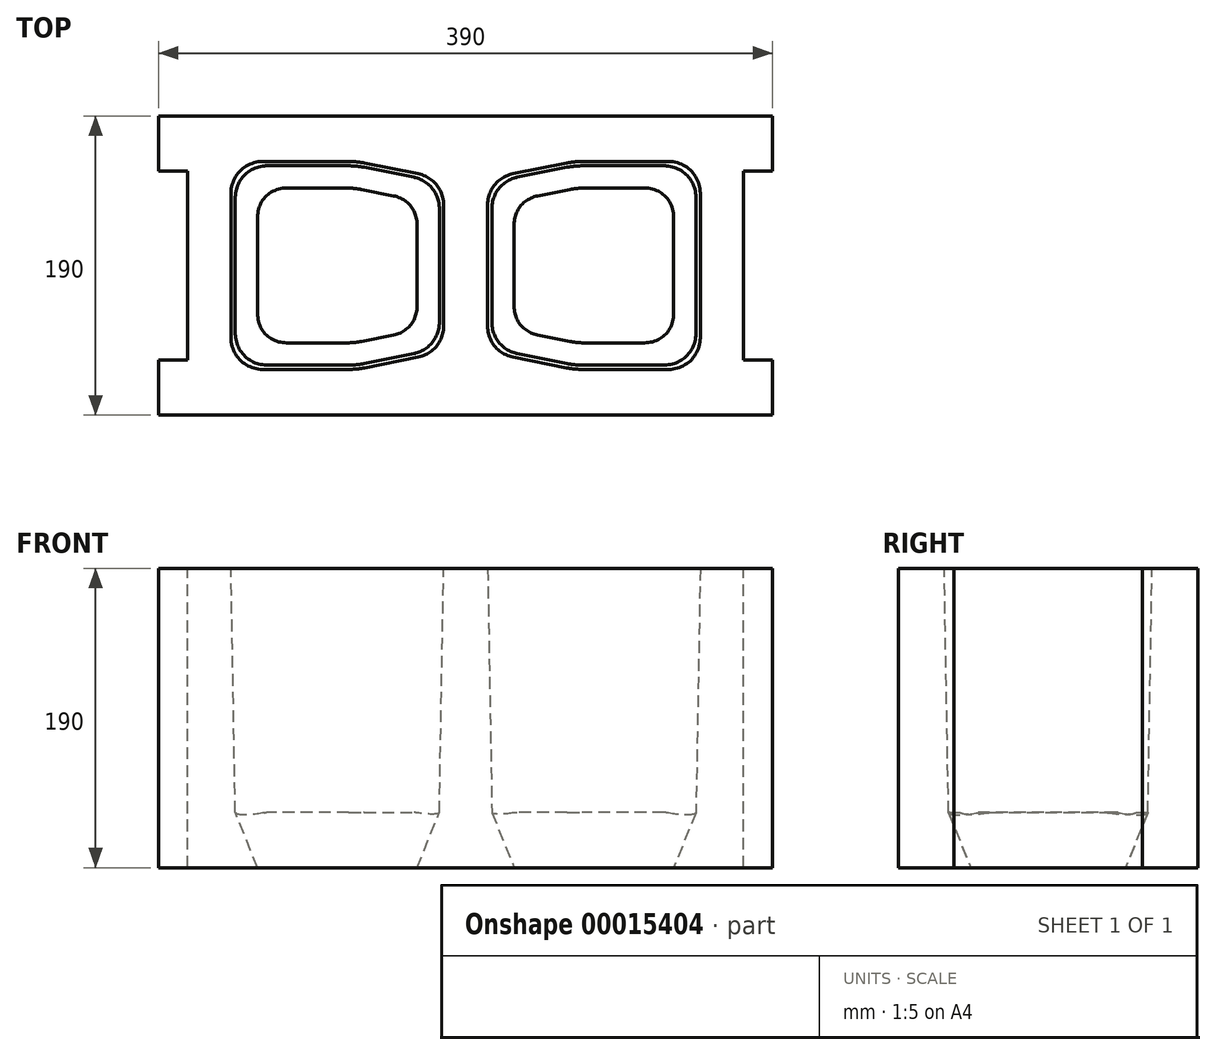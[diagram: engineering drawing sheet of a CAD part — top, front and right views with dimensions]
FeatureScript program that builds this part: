
annotation { "Feature Type Name" : "Feature", "Feature Type Description" : "" }
export const myFeature = defineFeature(function(context is Context, id is Id, definition is map)
    precondition{}
    {
        {
            var Q0;
            Q0=qCreatedBy(makeId("Top.planeOp"),FACE);
            var sketch = newSketch(context, id + "F0", { "sketchPlane" : qUnion([Q0])});
            skLineSegment(sketch, "E0.bottom", {"start": v(-195, 95) * mm, "end": v(195, 95) * mm});
            skLineSegment(sketch, "E0.top", {"start": v(-195, -95) * mm, "end": v(195, -95) * mm});
            skLineSegment(sketch, "E0.left", {"start": v(-195, 95) * mm, "end": v(-195, -95) * mm});
            skLineSegment(sketch, "E0.right", {"start": v(195, 95) * mm, "end": v(195, -95) * mm});
            skSolve(sketch);
        }
        {
            var Q0;
            Q0=qSketchRegion(id+"F0",true);
            extrude(context, id + "F1", {"entities" : qUnion([Q0]), "depth" : 190 * mm});
        }
        {
            var Q0;
            Q0=makeQuery(id+"F1.opExtrude","CAP_FACE",FACE,{"disambiguationData":[OSD([sQuery(id+"F0.wireOp",EDGE,"E0.bottom"),sQuery(id+"F0.wireOp",EDGE,"E0.top"),sQuery(id+"F0.wireOp",EDGE,"E0.left"),sQuery(id+"F0.wireOp",EDGE,"E0.right")])],"isStart":false});
            var sketch = newSketch(context, id + "F2", { "sketchPlane" : qUnion([Q0])});
            skLineSegment(sketch, "E1.bottom", {"start": v(-195, 83) * mm, "end": v(-191, 83) * mm});
            skLineSegment(sketch, "E1.top", {"start": v(-195, 71) * mm, "end": v(-191, 71) * mm});
            skLineSegment(sketch, "E1.left", {"start": v(-195, 83) * mm, "end": v(-195, 71) * mm});
            skLineSegment(sketch, "E1.right", {"start": v(-191, 83) * mm, "end": v(-191, 71) * mm});
            skSolve(sketch);
        }
        {
            var Q0;
            Q0=makeQuery(id+"F1.opExtrude","CAP_FACE",FACE,{"disambiguationData":[OSD([sQuery(id+"F0.wireOp",EDGE,"E0.bottom"),sQuery(id+"F0.wireOp",EDGE,"E0.top"),sQuery(id+"F0.wireOp",EDGE,"E0.left"),sQuery(id+"F0.wireOp",EDGE,"E0.right")])],"isStart":false});
            var sketch = newSketch(context, id + "F3", { "sketchPlane" : qUnion([Q0])});
            skLineSegment(sketch, "E2.bottom", {"start": v(-195, -71) * mm, "end": v(-191, -71) * mm});
            skLineSegment(sketch, "E2.top", {"start": v(-195, -83) * mm, "end": v(-191, -83) * mm});
            skLineSegment(sketch, "E2.left", {"start": v(-195, -71) * mm, "end": v(-195, -83) * mm});
            skLineSegment(sketch, "E2.right", {"start": v(-191, -71) * mm, "end": v(-191, -83) * mm});
            skLineSegment(sketch, "E3.MirrorCS", {"start": v(195, -83) * mm, "end": v(191, -83) * mm});
            skLineSegment(sketch, "E4.MirrorCS", {"start": v(195, -71) * mm, "end": v(191, -71) * mm});
            skLineSegment(sketch, "E5.MirrorCS", {"start": v(191, -71) * mm, "end": v(191, -83) * mm});
            skLineSegment(sketch, "E6.MirrorCS", {"start": v(195, -71) * mm, "end": v(195, -83) * mm});
            skLineSegment(sketch, "E7.MirrorCS", {"start": v(195, 71) * mm, "end": v(191, 71) * mm});
            skLineSegment(sketch, "E8.MirrorCS", {"start": v(191, 71) * mm, "end": v(191, 83) * mm});
            skLineSegment(sketch, "E9.MirrorCS", {"start": v(195, 71) * mm, "end": v(195, 83) * mm});
            skLineSegment(sketch, "E10.MirrorCS", {"start": v(195, 83) * mm, "end": v(191, 83) * mm});
            skSolve(sketch);
        }
        {
            var Q0;
            Q0=makeQuery(id+"F1.opExtrude","CAP_FACE",FACE,{"disambiguationData":[OSD([sQuery(id+"F0.wireOp",EDGE,"E0.bottom"),sQuery(id+"F0.wireOp",EDGE,"E0.top"),sQuery(id+"F0.wireOp",EDGE,"E0.left"),sQuery(id+"F0.wireOp",EDGE,"E0.right")])],"isStart":false});
            var sketch = newSketch(context, id + "F4", { "sketchPlane" : qUnion([Q0])});
            skLineSegment(sketch, "E11.bottom", {"start": v(-195, 60) * mm, "end": v(-176.5, 60) * mm});
            skLineSegment(sketch, "E11.top", {"start": v(-195, -60) * mm, "end": v(-176.5, -60) * mm});
            skLineSegment(sketch, "E11.left", {"start": v(-195, 60) * mm, "end": v(-195, -60) * mm});
            skLineSegment(sketch, "E11.right", {"start": v(-176.5, 60) * mm, "end": v(-176.5, -60) * mm});
            skLineSegment(sketch, "E12.MirrorCS", {"start": v(195, 60) * mm, "end": v(176.5, 60) * mm});
            skLineSegment(sketch, "E13.MirrorCS", {"start": v(195, -60) * mm, "end": v(176.5, -60) * mm});
            skLineSegment(sketch, "E14.MirrorCS", {"start": v(195, 60) * mm, "end": v(195, -60) * mm});
            skLineSegment(sketch, "E15.MirrorCS", {"start": v(176.5, 60) * mm, "end": v(176.5, -60) * mm});
            skSolve(sketch);
        }
        {
            var Q0;
            Q0=makeQuery(id+"F4.imprint","IMPRINT",FACE,{"disambiguationData":[TD([[makeQuery(id+"F4.imprint","IMPRINT",EDGE,{"derivedFrom":sQuery(id+"F4.wireOp",EDGE,"E12.MirrorCS")}),1.0]])]});
            var Q1;
            Q1=makeQuery(id+"F4.imprint","IMPRINT",FACE,{"disambiguationData":[TD([[makeQuery(id+"F4.imprint","IMPRINT",EDGE,{"derivedFrom":sQuery(id+"F4.wireOp",EDGE,"E11.bottom")}),-1.0]])]});
            extrude(context, id + "F5", {"entities" : qUnion([Q0, Q1]), "operationType" : NewBodyOperationType.REMOVE, "endBound" : BoundingType.THROUGH_ALL, "oppositeDirection" : true, "depth" : 25 * mm});
        }
        {
            var Q0;
            Q0=makeQuery(id+"F1.opExtrude","CAP_FACE",FACE,{"disambiguationData":[OSD([sQuery(id+"F0.wireOp",EDGE,"E0.bottom"),sQuery(id+"F0.wireOp",EDGE,"E0.top"),sQuery(id+"F0.wireOp",EDGE,"E0.left"),sQuery(id+"F0.wireOp",EDGE,"E0.right")])],"isStart":false});
            var sketch = newSketch(context, id + "F6", { "sketchPlane" : qUnion([Q0])});
            skLineSegment(sketch, "E16", {"start": v(-149, 66) * mm, "end": v(-149, -66) * mm});
            skLineSegment(sketch, "E17", {"start": v(-149, -66) * mm, "end": v(-69, -66) * mm});
            skLineSegment(sketch, "E18", {"start": v(-69, -66) * mm, "end": v(-14, -55) * mm});
            skLineSegment(sketch, "E19", {"start": v(-14, -55) * mm, "end": v(-14, 55) * mm});
            skLineSegment(sketch, "E20", {"start": v(-14, 55) * mm, "end": v(-69, 66) * mm});
            skLineSegment(sketch, "E21", {"start": v(-69, 66) * mm, "end": v(-149, 66) * mm});
            skLineSegment(sketch, "E22.MirrorCS", {"start": v(149, 66) * mm, "end": v(149, -66) * mm});
            skLineSegment(sketch, "E23.MirrorCS", {"start": v(149, -66) * mm, "end": v(69, -66) * mm});
            skLineSegment(sketch, "E24.MirrorCS", {"start": v(69, -66) * mm, "end": v(14, -55) * mm});
            skLineSegment(sketch, "E25.MirrorCS", {"start": v(69, 66) * mm, "end": v(149, 66) * mm});
            skLineSegment(sketch, "E26.MirrorCS", {"start": v(14, 55) * mm, "end": v(69, 66) * mm});
            skLineSegment(sketch, "E27.MirrorCS", {"start": v(14, -55) * mm, "end": v(14, 55) * mm});
            skSolve(sketch);
        }
        {
            var Q0;
            Q0=makeQuery(id+"F6.imprint","IMPRINT",FACE,{"disambiguationData":[TD([[makeQuery(id+"F6.imprint","IMPRINT",EDGE,{"derivedFrom":sQuery(id+"F6.wireOp",EDGE,"E22.MirrorCS")}),-1.0]])]});
            var Q1;
            Q1=makeQuery(id+"F6.imprint","IMPRINT",FACE,{"disambiguationData":[TD([[makeQuery(id+"F6.imprint","IMPRINT",EDGE,{"derivedFrom":sQuery(id+"F6.wireOp",EDGE,"E16")}),1.0]])]});
            extrude(context, id + "F7", {"entities" : qUnion([Q0, Q1]), "operationType" : NewBodyOperationType.REMOVE, "oppositeDirection" : true, "depth" : 155 * mm, "hasDraft" : true, "draftAngle" : 1 * degree, "draftPullDirection" : true});
        }
        {
            var Q0;
            Q0=makeQuery(id+"F7.boolean.opBoolean","COPY",FACE,{"derivedFrom":makeQuery(id+"F7.opExtrude","CAP_FACE",FACE,{"disambiguationData":[OSD([sQuery(id+"F6.wireOp",EDGE,"E22.MirrorCS"),sQuery(id+"F6.wireOp",EDGE,"E23.MirrorCS"),sQuery(id+"F6.wireOp",EDGE,"E24.MirrorCS"),sQuery(id+"F6.wireOp",EDGE,"E25.MirrorCS"),sQuery(id+"F6.wireOp",EDGE,"E26.MirrorCS"),sQuery(id+"F6.wireOp",EDGE,"E27.MirrorCS")])],"isStart":false})});
            extrude(context, id + "F8", {"entities" : qUnion([Q0]), "operationType" : NewBodyOperationType.REMOVE, "endBound" : BoundingType.THROUGH_ALL, "oppositeDirection" : true, "depth" : 25 * mm, "hasDraft" : true, "draftAngle" : 22 * degree, "draftPullDirection" : true});
        }
        {
            var Q0;
            Q0=makeQuery(id+"F7.boolean.opBoolean","COPY",FACE,{"derivedFrom":makeQuery(id+"F7.opExtrude","CAP_FACE",FACE,{"disambiguationData":[OSD([sQuery(id+"F6.wireOp",EDGE,"E16"),sQuery(id+"F6.wireOp",EDGE,"E17"),sQuery(id+"F6.wireOp",EDGE,"E18"),sQuery(id+"F6.wireOp",EDGE,"E19"),sQuery(id+"F6.wireOp",EDGE,"E20"),sQuery(id+"F6.wireOp",EDGE,"E21")])],"isStart":false})});
            extrude(context, id + "F9", {"entities" : qUnion([Q0]), "operationType" : NewBodyOperationType.REMOVE, "endBound" : BoundingType.THROUGH_ALL, "oppositeDirection" : true, "depth" : 25 * mm, "hasDraft" : true, "draftAngle" : 22 * degree, "draftPullDirection" : true});
        }
        {
            var Q0;
            Q0=makeQuery(id+"F7.boolean.opBoolean","COPY",EDGE,{"derivedFrom":makeQuery(id+"F7.opExtrude","SWEPT_EDGE",EDGE,{"disambiguationData":[OSD([sQuery(id+"F6.wireOp",EDGE,"E24.MirrorCS"),sQuery(id+"F6.wireOp",EDGE,"E27.MirrorCS")])]})});
            var Q1;
            Q1=makeQuery(id+"F7.boolean.opBoolean","COPY",EDGE,{"derivedFrom":makeQuery(id+"F7.opExtrude","SWEPT_EDGE",EDGE,{"disambiguationData":[OSD([sQuery(id+"F6.wireOp",EDGE,"E16"),sQuery(id+"F6.wireOp",EDGE,"E17")])]})});
            var Q2;
            Q2=makeQuery(id+"F7.boolean.opBoolean","COPY",EDGE,{"derivedFrom":makeQuery(id+"F7.opExtrude","SWEPT_EDGE",EDGE,{"disambiguationData":[OSD([sQuery(id+"F6.wireOp",EDGE,"E16"),sQuery(id+"F6.wireOp",EDGE,"E21")])]})});
            var Q3;
            Q3=makeQuery(id+"F7.boolean.opBoolean","COPY",EDGE,{"derivedFrom":makeQuery(id+"F7.opExtrude","SWEPT_EDGE",EDGE,{"disambiguationData":[OSD([sQuery(id+"F6.wireOp",EDGE,"E26.MirrorCS"),sQuery(id+"F6.wireOp",EDGE,"E27.MirrorCS")])]})});
            var Q4;
            Q4=makeQuery(id+"F7.boolean.opBoolean","COPY",EDGE,{"derivedFrom":makeQuery(id+"F7.opExtrude","SWEPT_EDGE",EDGE,{"disambiguationData":[OSD([sQuery(id+"F6.wireOp",EDGE,"E18"),sQuery(id+"F6.wireOp",EDGE,"E19")])]})});
            var Q5;
            Q5=makeQuery(id+"F7.boolean.opBoolean","COPY",EDGE,{"derivedFrom":makeQuery(id+"F7.opExtrude","SWEPT_EDGE",EDGE,{"disambiguationData":[OSD([sQuery(id+"F6.wireOp",EDGE,"E22.MirrorCS"),sQuery(id+"F6.wireOp",EDGE,"E23.MirrorCS")])]})});
            var Q6;
            Q6=makeQuery(id+"F7.boolean.opBoolean","COPY",EDGE,{"derivedFrom":makeQuery(id+"F7.opExtrude","SWEPT_EDGE",EDGE,{"disambiguationData":[OSD([sQuery(id+"F6.wireOp",EDGE,"E22.MirrorCS"),sQuery(id+"F6.wireOp",EDGE,"E25.MirrorCS")])]})});
            var Q7;
            Q7=makeQuery(id+"F7.boolean.opBoolean","COPY",EDGE,{"derivedFrom":makeQuery(id+"F7.opExtrude","SWEPT_EDGE",EDGE,{"disambiguationData":[OSD([sQuery(id+"F6.wireOp",EDGE,"E19"),sQuery(id+"F6.wireOp",EDGE,"E20")])]})});
            var Q8;
            Q8=makeQuery(id+"F9.boolean.opBoolean","COPY",EDGE,{"derivedFrom":makeQuery(id+"F9.opExtrude","SWEPT_EDGE",EDGE,{"disambiguationData":[OSD([sQuery(id+"F6.wireOp",EDGE,"E19"),sQuery(id+"F6.wireOp",EDGE,"E20")])]})});
            var Q9;
            Q9=makeQuery(id+"F8.boolean.opBoolean","COPY",EDGE,{"derivedFrom":makeQuery(id+"F8.opExtrude","SWEPT_EDGE",EDGE,{"disambiguationData":[OSD([sQuery(id+"F6.wireOp",EDGE,"E22.MirrorCS"),sQuery(id+"F6.wireOp",EDGE,"E25.MirrorCS")])]})});
            var Q10;
            Q10=makeQuery(id+"F8.boolean.opBoolean","COPY",EDGE,{"derivedFrom":makeQuery(id+"F8.opExtrude","SWEPT_EDGE",EDGE,{"disambiguationData":[OSD([sQuery(id+"F6.wireOp",EDGE,"E26.MirrorCS"),sQuery(id+"F6.wireOp",EDGE,"E27.MirrorCS")])]})});
            var Q11;
            Q11=makeQuery(id+"F9.boolean.opBoolean","COPY",EDGE,{"derivedFrom":makeQuery(id+"F9.opExtrude","SWEPT_EDGE",EDGE,{"disambiguationData":[OSD([sQuery(id+"F6.wireOp",EDGE,"E16"),sQuery(id+"F6.wireOp",EDGE,"E21")])]})});
            var Q12;
            Q12=makeQuery(id+"F8.boolean.opBoolean","COPY",EDGE,{"derivedFrom":makeQuery(id+"F8.opExtrude","SWEPT_EDGE",EDGE,{"disambiguationData":[OSD([sQuery(id+"F6.wireOp",EDGE,"E22.MirrorCS"),sQuery(id+"F6.wireOp",EDGE,"E23.MirrorCS")])]})});
            var Q13;
            Q13=makeQuery(id+"F9.boolean.opBoolean","COPY",EDGE,{"derivedFrom":makeQuery(id+"F9.opExtrude","SWEPT_EDGE",EDGE,{"disambiguationData":[OSD([sQuery(id+"F6.wireOp",EDGE,"E18"),sQuery(id+"F6.wireOp",EDGE,"E19")])]})});
            var Q14;
            Q14=makeQuery(id+"F9.boolean.opBoolean","COPY",EDGE,{"derivedFrom":makeQuery(id+"F9.opExtrude","SWEPT_EDGE",EDGE,{"disambiguationData":[OSD([sQuery(id+"F6.wireOp",EDGE,"E16"),sQuery(id+"F6.wireOp",EDGE,"E17")])]})});
            var Q15;
            Q15=makeQuery(id+"F8.boolean.opBoolean","COPY",EDGE,{"derivedFrom":makeQuery(id+"F8.opExtrude","SWEPT_EDGE",EDGE,{"disambiguationData":[OSD([sQuery(id+"F6.wireOp",EDGE,"E24.MirrorCS"),sQuery(id+"F6.wireOp",EDGE,"E27.MirrorCS")])]})});
            fillet(context, id + "F10", {"entities" : qUnion([Q0, Q1, Q2, Q3, Q4, Q5, Q6, Q7, Q8, Q9, Q10, Q11, Q12, Q13, Q14, Q15]), "radius" : 20 * mm, "tangentPropagation" : true, "allowEdgeOverflow" : false});
        }
        {
            var Q0;
            Q0=makeQuery(id+"F7.boolean.opBoolean","COPY",EDGE,{"derivedFrom":makeQuery(id+"F7.opExtrude","SWEPT_EDGE",EDGE,{"disambiguationData":[OSD([sQuery(id+"F6.wireOp",EDGE,"E23.MirrorCS"),sQuery(id+"F6.wireOp",EDGE,"E24.MirrorCS")])]})});
            var Q1;
            Q1=makeQuery(id+"F8.boolean.opBoolean","COPY",EDGE,{"derivedFrom":makeQuery(id+"F8.opExtrude","SWEPT_EDGE",EDGE,{"disambiguationData":[OSD([sQuery(id+"F6.wireOp",EDGE,"E23.MirrorCS"),sQuery(id+"F6.wireOp",EDGE,"E24.MirrorCS")])]})});
            var Q2;
            Q2=makeQuery(id+"F7.boolean.opBoolean","COPY",EDGE,{"derivedFrom":makeQuery(id+"F7.opExtrude","SWEPT_EDGE",EDGE,{"disambiguationData":[OSD([sQuery(id+"F6.wireOp",EDGE,"E17"),sQuery(id+"F6.wireOp",EDGE,"E18")])]})});
            var Q3;
            Q3=makeQuery(id+"F9.boolean.opBoolean","COPY",EDGE,{"derivedFrom":makeQuery(id+"F9.opExtrude","SWEPT_EDGE",EDGE,{"disambiguationData":[OSD([sQuery(id+"F6.wireOp",EDGE,"E17"),sQuery(id+"F6.wireOp",EDGE,"E18")])]})});
            var Q4;
            Q4=makeQuery(id+"F9.boolean.opBoolean","COPY",EDGE,{"derivedFrom":makeQuery(id+"F9.opExtrude","SWEPT_EDGE",EDGE,{"disambiguationData":[OSD([sQuery(id+"F6.wireOp",EDGE,"E20"),sQuery(id+"F6.wireOp",EDGE,"E21")])]})});
            var Q5;
            Q5=makeQuery(id+"F7.boolean.opBoolean","COPY",EDGE,{"derivedFrom":makeQuery(id+"F7.opExtrude","SWEPT_EDGE",EDGE,{"disambiguationData":[OSD([sQuery(id+"F6.wireOp",EDGE,"E20"),sQuery(id+"F6.wireOp",EDGE,"E21")])]})});
            var Q6;
            Q6=makeQuery(id+"F8.boolean.opBoolean","COPY",EDGE,{"derivedFrom":makeQuery(id+"F8.opExtrude","SWEPT_EDGE",EDGE,{"disambiguationData":[OSD([sQuery(id+"F6.wireOp",EDGE,"E25.MirrorCS"),sQuery(id+"F6.wireOp",EDGE,"E26.MirrorCS")])]})});
            var Q7;
            Q7=makeQuery(id+"F7.boolean.opBoolean","COPY",EDGE,{"derivedFrom":makeQuery(id+"F7.opExtrude","SWEPT_EDGE",EDGE,{"disambiguationData":[OSD([sQuery(id+"F6.wireOp",EDGE,"E25.MirrorCS"),sQuery(id+"F6.wireOp",EDGE,"E26.MirrorCS")])]})});
            fillet(context, id + "F11", {"entities" : qUnion([Q0, Q1, Q2, Q3, Q4, Q5, Q6, Q7]), "radius" : 50 * mm, "tangentPropagation" : true, "allowEdgeOverflow" : false});
        }
    });
